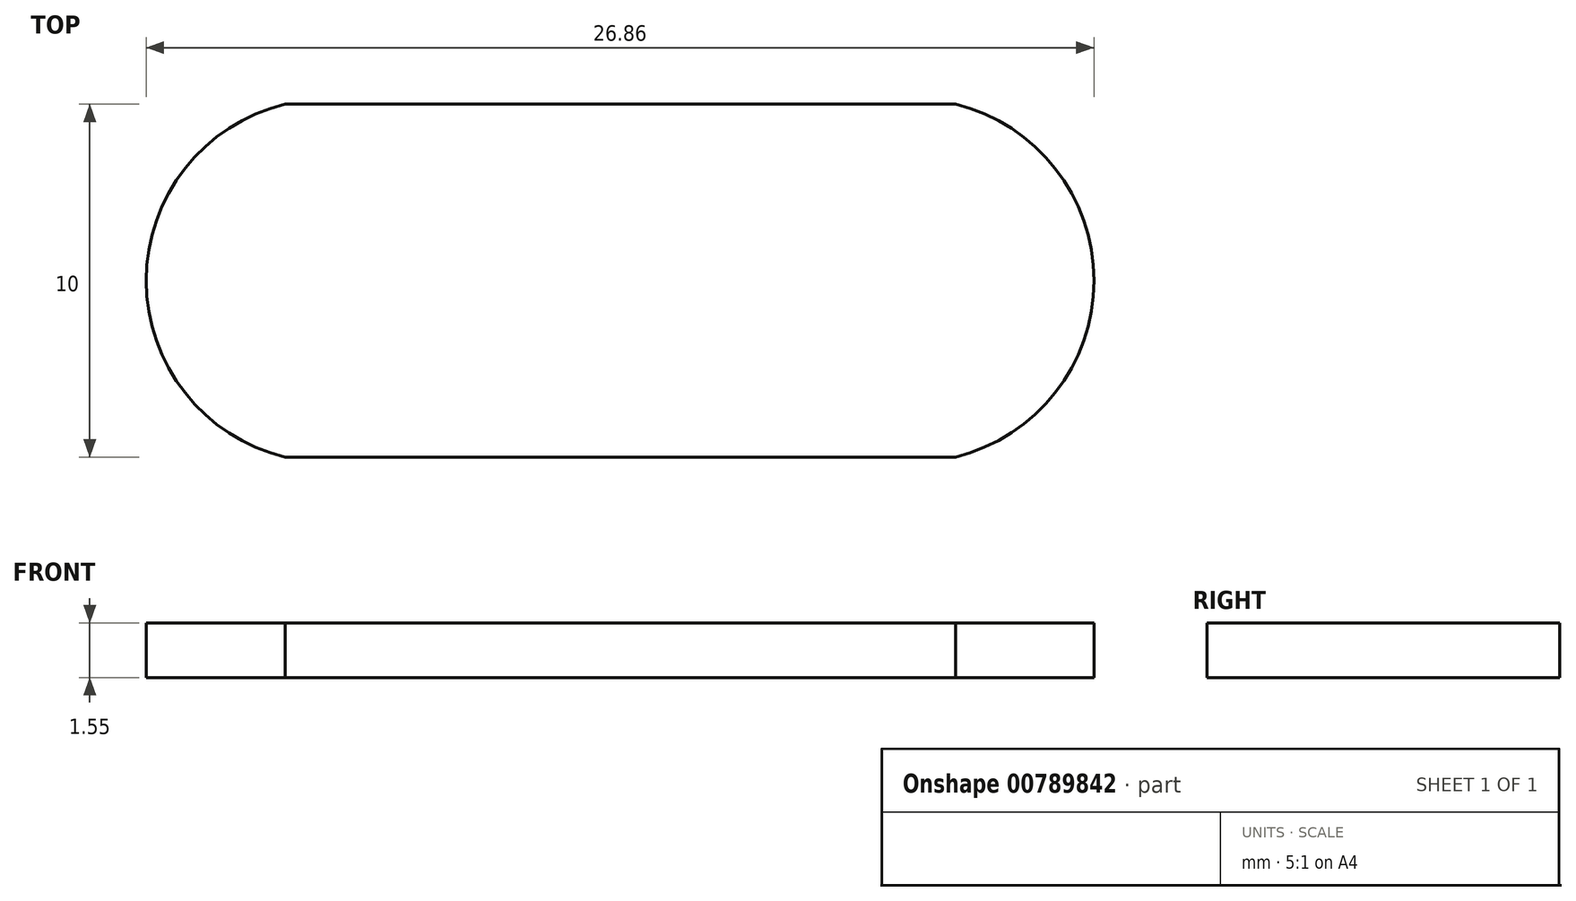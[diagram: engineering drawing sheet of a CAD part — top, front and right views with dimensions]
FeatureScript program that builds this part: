
annotation { "Feature Type Name" : "Feature", "Feature Type Description" : "" }
export const myFeature = defineFeature(function(context is Context, id is Id, definition is map)
    precondition{}
    {
        {
            var Q0;
            Q0=qCreatedBy(makeId("Top.planeOp"),FACE);
            var sketch = newSketch(context, id + "F0", { "sketchPlane" : qUnion([Q0])});
            skLineSegment(sketch, "E0.bottom", {"start": v(9.5, -5) * mm, "end": v(-9.5, -5) * mm});
            skLineSegment(sketch, "E0.top", {"start": v(9.5, 5) * mm, "end": v(-9.5, 5) * mm});
            skPoint(sketch, "E0.middle", {"position": v(0, 0) * mm});
            skLineSegment(sketch, "E1", {"start": v(-13.5, 16.08) * mm, "end": v(-13.5, -14.56) * mm, "construction": true});
            skLineSegment(sketch, "E2", {"start": v(13.5, 17.66) * mm, "end": v(13.5, -14.65) * mm, "construction": true});
            skArc(sketch, "E3", {"start": v(9.5, -5) * mm, "mid": v(13.42, 0) * mm, "end": v(9.5, 5) * mm});
            skArc(sketch, "E4", {"start": v(-9.5, 5) * mm, "mid": v(-13.44, 0) * mm, "end": v(-9.5, -5) * mm});
            skSolve(sketch);
        }
        {
            var Q0;
            Q0=makeQuery(id+"F0.imprint","IMPRINT",FACE,{"disambiguationData":[TD([[makeQuery(id+"F0.imprint","IMPRINT",EDGE,{"derivedFrom":sQuery(id+"F0.wireOp",EDGE,"E0.bottom")}),-1.0]])]});
            extrude(context, id + "F1", {"entities" : qUnion([Q0]), "depth" : 1 * mm, "offsetDistance" : 25 * mm});
        }
        {
            var Q0;
            Q0=makeQuery(id+"F1.opExtrude","CAP_FACE",FACE,{"disambiguationData":[OSD([sQuery(id+"F0.wireOp",EDGE,"E0.bottom"),sQuery(id+"F0.wireOp",EDGE,"E0.top"),sQuery(id+"F0.wireOp",EDGE,"E3"),sQuery(id+"F0.wireOp",EDGE,"E4"),sQuery(id+"F0.wireOp",EDGE,"GkiCUaz8-CI8J-PPwi-A7GH-rB4C0vrd3rIn")])],"isStart":false});
            var sketch = newSketch(context, id + "F2", { "sketchPlane" : qUnion([Q0])});
            skArc(sketch, "E5.0", {"start": v(-9.5, 5) * mm, "mid": v(-13.44, 0) * mm, "end": v(-9.5, -5) * mm});
            skLineSegment(sketch, "E5.1", {"start": v(9.5, -5) * mm, "end": v(-9.5, -5) * mm});
            skArc(sketch, "E5.2", {"start": v(9.5, -5) * mm, "mid": v(13.42, 0) * mm, "end": v(9.5, 5) * mm});
            skLineSegment(sketch, "E5.3", {"start": v(9.5, 5) * mm, "end": v(-9.5, 5) * mm});
            skSolve(sketch);
        }
        {
            var Q0;
            Q0=qSketchRegion(id+"F2",true);
            extrude(context, id + "F3", {"entities" : qUnion([Q0]), "operationType" : NewBodyOperationType.ADD, "depth" : 0.55 * mm, "offsetDistance" : 25 * mm});
        }
    });
